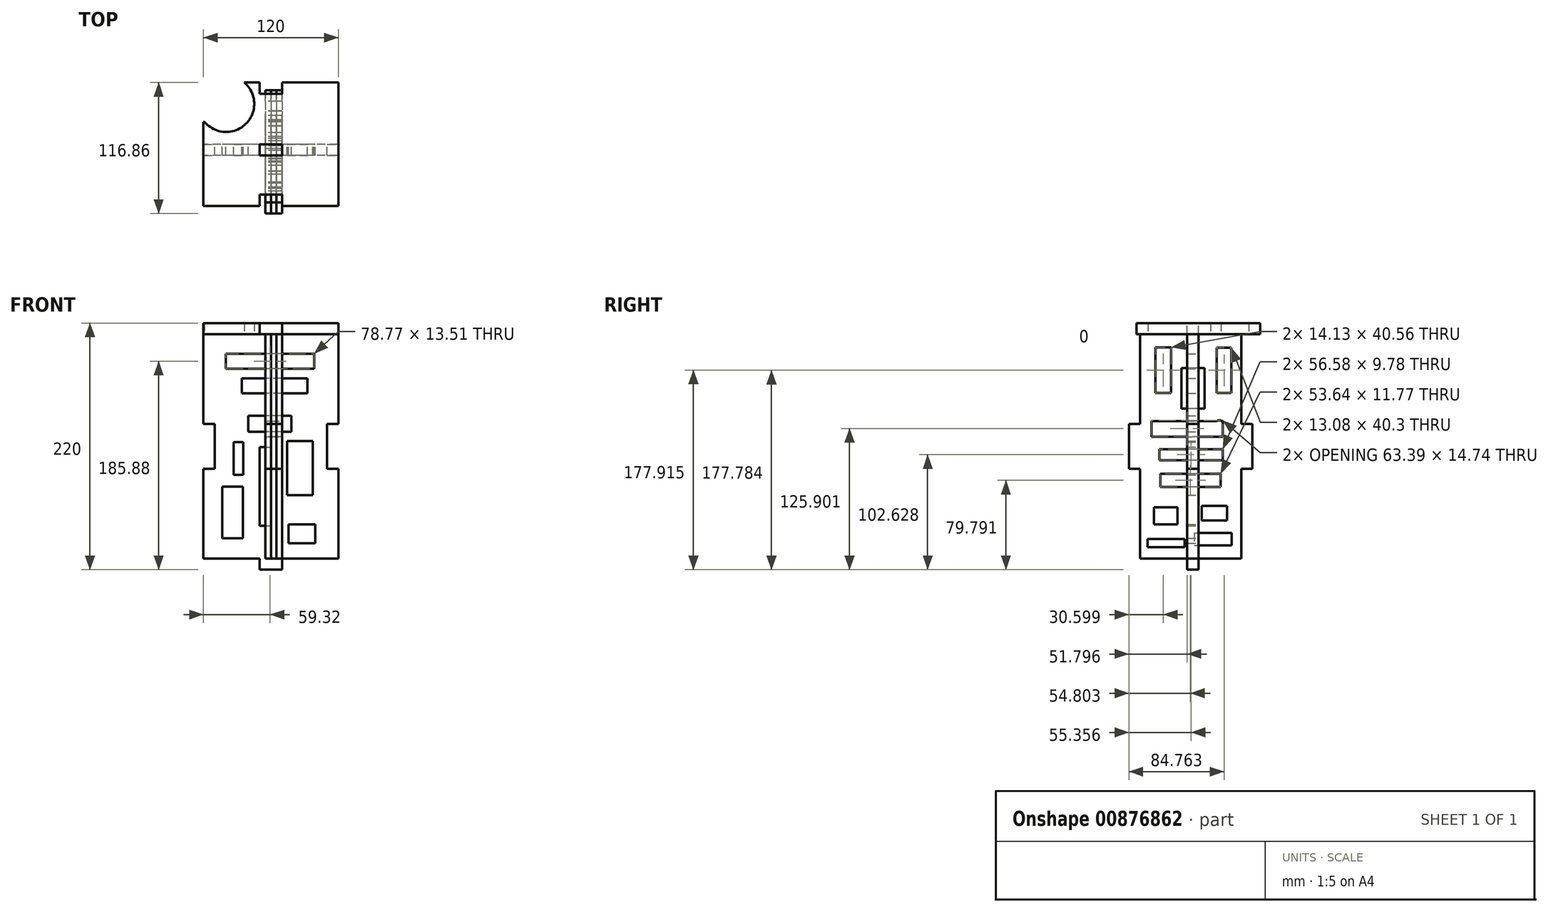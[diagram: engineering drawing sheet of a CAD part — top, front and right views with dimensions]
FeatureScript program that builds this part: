
annotation { "Feature Type Name" : "Feature", "Feature Type Description" : "" }
export const myFeature = defineFeature(function(context is Context, id is Id, definition is map)
    precondition{}
    {
        {
            var Q0;
            Q0=qCreatedBy(makeId("Top.planeOp"),FACE);
            var sketch = newSketch(context, id + "F0", { "sketchPlane" : qUnion([Q0])});
            skLineSegment(sketch, "E0.bottom", {"start": v(-60, -55) * mm, "end": v(-10, -55) * mm});
            skLineSegment(sketch, "E0.left", {"start": v(-60, -55) * mm, "end": v(-60, 21.17) * mm});
            skLineSegment(sketch, "E0.right", {"start": v(60, -55) * mm, "end": v(60, 55) * mm});
            skPoint(sketch, "E0.middle", {"position": v(0, 0) * mm});
            skLineSegment(sketch, "E1.bottom", {"start": v(-10, 45) * mm, "end": v(10, 45) * mm});
            skLineSegment(sketch, "E1.left", {"start": v(-10, 45) * mm, "end": v(-10, 55) * mm});
            skLineSegment(sketch, "E1.right", {"start": v(10, 45) * mm, "end": v(10, 55) * mm});
            skPoint(sketch, "E1.middle", {"position": v(0, 55) * mm});
            skPoint(sketch, "E1.top.end.orphan", {"position": v(10, 65) * mm});
            skPoint(sketch, "E2.orphan", {"position": v(-10, 65) * mm});
            skLineSegment(sketch, "E3.trimOffspring", {"start": v(10, 55) * mm, "end": v(60, 55) * mm});
            skLineSegment(sketch, "E4.bottom", {"start": v(-10, -45) * mm, "end": v(10, -45) * mm});
            skLineSegment(sketch, "E4.left", {"start": v(-10, -45) * mm, "end": v(-10, -55) * mm});
            skLineSegment(sketch, "E4.right", {"start": v(10, -45) * mm, "end": v(10, -55) * mm});
            skPoint(sketch, "E4.middle", {"position": v(0, -55) * mm});
            skPoint(sketch, "E5.orphan", {"position": v(10, -65) * mm});
            skPoint(sketch, "E6.orphan", {"position": v(-10, -65) * mm});
            skLineSegment(sketch, "E7.trimOffspring", {"start": v(10, -55) * mm, "end": v(60, -55) * mm});
            skLineSegment(sketch, "E8", {"start": v(-59.1, 20) * mm, "end": v(-60, 20) * mm});
            skArc(sketch, "E9.trimOffspring", {"start": v(-60, 21.17) * mm, "mid": v(-22.8, 17.63) * mm, "end": v(-23.66, 55) * mm});
            skLineSegment(sketch, "E10.trimOffspring", {"start": v(-23.66, 55) * mm, "end": v(-10, 55) * mm});
            skPoint(sketch, "E11.orphan", {"position": v(-25, 20) * mm});
            skPoint(sketch, "E0.top.start.orphan", {"position": v(-60, 55) * mm});
            skLineSegment(sketch, "E12", {"start": v(-23.66, 55) * mm, "end": v(-60, 55) * mm, "construction": true});
            skLineSegment(sketch, "E13", {"start": v(-60, 21.17) * mm, "end": v(-60, 55) * mm, "construction": true});
            skSolve(sketch);
        }
        {
            var Q0;
            {var subQ1=sQuery(id+"F0.wireOp",EDGE,"E0.bottom");Q0=makeQuery(id+"F0.imprint","IMPRINT",FACE,{"disambiguationData":[TD([[makeQuery(id+"F0.imprint","IMPRINT",EDGE,{"derivedFrom":subQ1}),1.0]])]});}
            extrude(context, id + "F1", {"entities" : qUnion([Q0]), "depth" : 10 * mm, "offsetDistance" : 25 * mm});
        }
        {
            var Q0;
            Q0=qCreatedBy(makeId("Front.planeOp"),FACE);
            var sketch = newSketch(context, id + "F2", { "sketchPlane" : qUnion([Q0])});
            skLineSegment(sketch, "E14.bottom", {"start": v(60, 0) * mm, "end": v(10, 0) * mm});
            skLineSegment(sketch, "E14.top", {"start": v(60, -200) * mm, "end": v(10, -200) * mm});
            skLineSegment(sketch, "E14.left", {"start": v(60, 0) * mm, "end": v(60, -80) * mm});
            skLineSegment(sketch, "E14.right", {"start": v(-60, 0) * mm, "end": v(-60, -80) * mm});
            skLineSegment(sketch, "E15.top", {"start": v(-10, 10) * mm, "end": v(10, 10) * mm});
            skLineSegment(sketch, "E15.left", {"start": v(-10, 0) * mm, "end": v(-10, 10) * mm});
            skLineSegment(sketch, "E15.right", {"start": v(10, 0) * mm, "end": v(10, 10) * mm});
            skPoint(sketch, "E15.middle", {"position": v(0, 0) * mm});
            skPoint(sketch, "E16.orphan", {"position": v(-10, -10) * mm});
            skPoint(sketch, "E17.orphan", {"position": v(10, -10) * mm});
            skLineSegment(sketch, "E18.top", {"start": v(-10, -210) * mm, "end": v(10, -210) * mm});
            skLineSegment(sketch, "E18.left", {"start": v(-10, -200) * mm, "end": v(-10, -210) * mm});
            skLineSegment(sketch, "E18.right", {"start": v(10, -200) * mm, "end": v(10, -210) * mm});
            skPoint(sketch, "E18.middle", {"position": v(0, -200) * mm});
            skPoint(sketch, "E19.orphan", {"position": v(10, -190) * mm});
            skPoint(sketch, "E20.orphan", {"position": v(-10, -190) * mm});
            skLineSegment(sketch, "E21.trimOffspring", {"start": v(-10, -200) * mm, "end": v(-60, -200) * mm});
            skLineSegment(sketch, "E22.trimOffspring", {"start": v(-10, 0) * mm, "end": v(-60, 0) * mm});
            skLineSegment(sketch, "E23.bottom", {"start": v(50, -80) * mm, "end": v(60, -80) * mm});
            skLineSegment(sketch, "E23.top", {"start": v(50, -120) * mm, "end": v(60, -120) * mm});
            skLineSegment(sketch, "E23.left", {"start": v(50, -80) * mm, "end": v(50, -120) * mm});
            skPoint(sketch, "E23.middle", {"position": v(60, -100) * mm});
            skLineSegment(sketch, "E24.trimOffspring", {"start": v(60, -120) * mm, "end": v(60, -200) * mm});
            skPoint(sketch, "E23.right.start.orphan", {"position": v(70, -80) * mm});
            skPoint(sketch, "E25.orphan", {"position": v(70, -120) * mm});
            skLineSegment(sketch, "E26.bottom", {"start": v(-60, -120) * mm, "end": v(-50, -120) * mm});
            skLineSegment(sketch, "E26.top", {"start": v(-60, -80) * mm, "end": v(-50, -80) * mm});
            skLineSegment(sketch, "E26.right", {"start": v(-50, -120) * mm, "end": v(-50, -80) * mm});
            skPoint(sketch, "E26.middle", {"position": v(-60, -100) * mm});
            skPoint(sketch, "E27.orphan", {"position": v(-70, -80) * mm});
            skPoint(sketch, "E28.orphan", {"position": v(-70, -120) * mm});
            skLineSegment(sketch, "E29.trimOffspring", {"start": v(-60, -120) * mm, "end": v(-60, -200) * mm});
            skLineSegment(sketch, "E30.bottom", {"start": v(38.7, -17.36) * mm, "end": v(-40.06, -17.36) * mm});
            skLineSegment(sketch, "E30.top", {"start": v(38.7, -30.88) * mm, "end": v(-40.06, -30.88) * mm});
            skLineSegment(sketch, "E30.left", {"start": v(38.7, -17.36) * mm, "end": v(38.7, -30.88) * mm});
            skLineSegment(sketch, "E30.right", {"start": v(-40.06, -17.36) * mm, "end": v(-40.06, -30.88) * mm});
            skLineSegment(sketch, "E31.bottom", {"start": v(32.44, -39.45) * mm, "end": v(-25.9, -39.45) * mm});
            skLineSegment(sketch, "E31.top", {"start": v(32.44, -52.63) * mm, "end": v(-25.9, -52.63) * mm});
            skLineSegment(sketch, "E31.left", {"start": v(32.44, -39.45) * mm, "end": v(32.44, -52.63) * mm});
            skLineSegment(sketch, "E31.right", {"start": v(-25.9, -39.45) * mm, "end": v(-25.9, -52.63) * mm});
            skLineSegment(sketch, "E32.bottom", {"start": v(18.27, -72.73) * mm, "end": v(-20.29, -72.73) * mm});
            skLineSegment(sketch, "E32.top", {"start": v(18.27, -86.9) * mm, "end": v(-20.29, -86.9) * mm});
            skLineSegment(sketch, "E32.left", {"start": v(18.27, -72.73) * mm, "end": v(18.27, -86.9) * mm});
            skLineSegment(sketch, "E32.right", {"start": v(-20.29, -72.73) * mm, "end": v(-20.29, -86.9) * mm});
            skLineSegment(sketch, "E33.bottom", {"start": v(-10.07, -100.75) * mm, "end": v(0, -100.75) * mm});
            skLineSegment(sketch, "E33.top", {"start": v(-10.07, -170.95) * mm, "end": v(0, -170.95) * mm});
            skLineSegment(sketch, "E33.left", {"start": v(-10.07, -100.75) * mm, "end": v(-10.07, -170.95) * mm});
            skLineSegment(sketch, "E33.right", {"start": v(0, -100.75) * mm, "end": v(0, -170.95) * mm});
            skLineSegment(sketch, "E34.bottom", {"start": v(14.32, -95.14) * mm, "end": v(37.39, -95.14) * mm});
            skLineSegment(sketch, "E34.top", {"start": v(14.32, -143.6) * mm, "end": v(37.39, -143.6) * mm});
            skLineSegment(sketch, "E34.left", {"start": v(14.32, -95.14) * mm, "end": v(14.32, -143.6) * mm});
            skLineSegment(sketch, "E34.right", {"start": v(37.39, -95.14) * mm, "end": v(37.39, -143.6) * mm});
            skLineSegment(sketch, "E35.bottom", {"start": v(-24.9, -136.01) * mm, "end": v(-43.36, -136.01) * mm});
            skLineSegment(sketch, "E35.top", {"start": v(-24.9, -181.82) * mm, "end": v(-43.36, -181.82) * mm});
            skLineSegment(sketch, "E35.left", {"start": v(-24.9, -136.01) * mm, "end": v(-24.9, -181.82) * mm});
            skLineSegment(sketch, "E35.right", {"start": v(-43.36, -136.01) * mm, "end": v(-43.36, -181.82) * mm});
            skLineSegment(sketch, "E36.bottom", {"start": v(39.36, -169.63) * mm, "end": v(15.63, -169.63) * mm});
            skLineSegment(sketch, "E36.top", {"start": v(39.36, -186.44) * mm, "end": v(15.63, -186.44) * mm});
            skLineSegment(sketch, "E36.left", {"start": v(39.36, -169.63) * mm, "end": v(39.36, -186.44) * mm});
            skLineSegment(sketch, "E36.right", {"start": v(15.63, -169.63) * mm, "end": v(15.63, -186.44) * mm});
            skLineSegment(sketch, "E37.bottom", {"start": v(-33.32, -96.04) * mm, "end": v(-24.61, -96.04) * mm});
            skLineSegment(sketch, "E37.top", {"start": v(-33.32, -125.28) * mm, "end": v(-24.61, -125.28) * mm});
            skLineSegment(sketch, "E37.left", {"start": v(-33.32, -96.04) * mm, "end": v(-33.32, -125.28) * mm});
            skLineSegment(sketch, "E37.right", {"start": v(-24.61, -96.04) * mm, "end": v(-24.61, -125.28) * mm});
            skSolve(sketch);
        }
        {
            var Q0;
            Q0 = qSketchRegion(id + "F2", true);
            extrude(context, id + "F3", {"entities" : qUnion([Q0]), "depth" : 10 * mm, "offsetDistance" : 25 * mm});
        }
        {
            var Q0;
            Q0=qCreatedBy(makeId("Right.planeOp"),FACE);
            var sketch = newSketch(context, id + "F4", { "sketchPlane" : qUnion([Q0])});
            skLineSegment(sketch, "E38.bottom", {"start": v(38.14, 0) * mm, "end": v(-51.86, 0) * mm});
            skLineSegment(sketch, "E38.top", {"start": v(38.14, -200) * mm, "end": v(-51.86, -200) * mm});
            skLineSegment(sketch, "E38.left", {"start": v(38.14, 0) * mm, "end": v(38.14, -80) * mm});
            skLineSegment(sketch, "E38.right", {"start": v(-51.86, 0) * mm, "end": v(-51.86, -80) * mm});
            skLineSegment(sketch, "E39", {"start": v(38.14, -80) * mm, "end": v(48.14, -80) * mm});
            skLineSegment(sketch, "E40", {"start": v(48.14, -80) * mm, "end": v(48.14, -120) * mm});
            skLineSegment(sketch, "E41", {"start": v(48.14, -120) * mm, "end": v(38.14, -120) * mm});
            skLineSegment(sketch, "E42.trimOffspring", {"start": v(38.14, -120) * mm, "end": v(38.14, -200) * mm});
            skLineSegment(sketch, "E43", {"start": v(-51.86, -80) * mm, "end": v(-61.86, -80) * mm});
            skLineSegment(sketch, "E44", {"start": v(-61.86, -80) * mm, "end": v(-61.86, -120) * mm});
            skLineSegment(sketch, "E45", {"start": v(-61.86, -120) * mm, "end": v(-51.86, -120) * mm});
            skLineSegment(sketch, "E46.trimOffspring", {"start": v(-51.86, -120) * mm, "end": v(-51.86, -200) * mm});
            skText(sketch, "E47", { "text": "YouSef", "fontName": "OpenSans-Regular.ttf"});
            skPoint(sketch, "E48.left.end.orphan", {"position": v(-15.86, -56.8) * mm});
            skPoint(sketch, "E49.bottom.start.orphan", {"position": v(-15.86, -107.95) * mm});
            skLineSegment(sketch, "E50.bottom", {"start": v(-41.76, -77.6) * mm, "end": v(21.63, -77.6) * mm});
            skLineSegment(sketch, "E50.top", {"start": v(-41.76, -91.28) * mm, "end": v(21.63, -91.28) * mm});
            skLineSegment(sketch, "E50.left", {"start": v(-41.76, -77.6) * mm, "end": v(-41.76, -91.28) * mm});
            skLineSegment(sketch, "E50.right", {"start": v(21.63, -77.6) * mm, "end": v(21.63, -91.28) * mm});
            skLineSegment(sketch, "E51.bottom", {"start": v(29.45, -12.07) * mm, "end": v(16.36, -12.07) * mm});
            skLineSegment(sketch, "E51.top", {"start": v(29.45, -52.36) * mm, "end": v(16.36, -52.36) * mm});
            skLineSegment(sketch, "E51.left", {"start": v(29.45, -12.07) * mm, "end": v(29.45, -52.36) * mm});
            skLineSegment(sketch, "E51.right", {"start": v(16.36, -12.07) * mm, "end": v(16.36, -52.36) * mm});
            skLineSegment(sketch, "E52.bottom", {"start": v(-38.33, -11.8) * mm, "end": v(-24.2, -11.8) * mm});
            skLineSegment(sketch, "E52.top", {"start": v(-38.33, -52.36) * mm, "end": v(-24.2, -52.36) * mm});
            skLineSegment(sketch, "E52.left", {"start": v(-38.33, -11.8) * mm, "end": v(-38.33, -52.36) * mm});
            skLineSegment(sketch, "E52.right", {"start": v(-24.2, -11.8) * mm, "end": v(-24.2, -52.36) * mm});
            skLineSegment(sketch, "E53.bottom", {"start": v(5.37, -30.12) * mm, "end": v(-15.04, -30.12) * mm});
            skLineSegment(sketch, "E53.top", {"start": v(5.37, -66.5) * mm, "end": v(-15.04, -66.5) * mm});
            skLineSegment(sketch, "E53.left", {"start": v(5.37, -30.12) * mm, "end": v(5.37, -66.5) * mm});
            skLineSegment(sketch, "E53.right", {"start": v(-15.04, -30.12) * mm, "end": v(-15.04, -66.5) * mm});
            skLineSegment(sketch, "E54.bottom", {"start": v(19.76, -124.32) * mm, "end": v(-33.88, -124.32) * mm});
            skLineSegment(sketch, "E54.top", {"start": v(19.76, -136.1) * mm, "end": v(-33.88, -136.1) * mm});
            skLineSegment(sketch, "E54.left", {"start": v(19.76, -124.32) * mm, "end": v(19.76, -136.1) * mm});
            skLineSegment(sketch, "E54.right", {"start": v(-33.88, -124.32) * mm, "end": v(-33.88, -136.1) * mm});
            skLineSegment(sketch, "E55.bottom", {"start": v(25.52, -153.1) * mm, "end": v(3.02, -153.1) * mm});
            skLineSegment(sketch, "E55.top", {"start": v(25.52, -165.93) * mm, "end": v(3.02, -165.93) * mm});
            skLineSegment(sketch, "E55.left", {"start": v(25.52, -153.1) * mm, "end": v(25.52, -165.93) * mm});
            skLineSegment(sketch, "E55.right", {"start": v(3.02, -153.1) * mm, "end": v(3.02, -165.93) * mm});
            skLineSegment(sketch, "E56.bottom", {"start": v(-18.7, -154.41) * mm, "end": v(-39.63, -154.41) * mm});
            skLineSegment(sketch, "E56.top", {"start": v(-18.7, -169.59) * mm, "end": v(-39.63, -169.59) * mm});
            skLineSegment(sketch, "E56.left", {"start": v(-18.7, -154.41) * mm, "end": v(-18.7, -169.59) * mm});
            skLineSegment(sketch, "E56.right", {"start": v(-39.63, -154.41) * mm, "end": v(-39.63, -169.59) * mm});
            skLineSegment(sketch, "E57.bottom", {"start": v(-3.79, -177.18) * mm, "end": v(29.7, -177.18) * mm});
            skLineSegment(sketch, "E57.top", {"start": v(-3.79, -188.17) * mm, "end": v(29.7, -188.17) * mm});
            skLineSegment(sketch, "E57.left", {"start": v(-3.79, -177.18) * mm, "end": v(-3.79, -188.17) * mm});
            skLineSegment(sketch, "E57.right", {"start": v(29.7, -177.18) * mm, "end": v(29.7, -188.17) * mm});
            skLineSegment(sketch, "E58.bottom", {"start": v(-45.4, -182.67) * mm, "end": v(-12.42, -182.67) * mm});
            skLineSegment(sketch, "E58.top", {"start": v(-45.4, -190) * mm, "end": v(-12.42, -190) * mm});
            skLineSegment(sketch, "E58.left", {"start": v(-45.4, -182.67) * mm, "end": v(-45.4, -190) * mm});
            skLineSegment(sketch, "E58.right", {"start": v(-12.42, -182.67) * mm, "end": v(-12.42, -190) * mm});
            skLineSegment(sketch, "E59.bottom", {"start": v(21.79, -102.48) * mm, "end": v(-34.8, -102.48) * mm});
            skLineSegment(sketch, "E59.top", {"start": v(21.79, -112.26) * mm, "end": v(-34.8, -112.26) * mm});
            skLineSegment(sketch, "E59.left", {"start": v(21.79, -102.48) * mm, "end": v(21.79, -112.26) * mm});
            skLineSegment(sketch, "E59.right", {"start": v(-34.8, -102.48) * mm, "end": v(-34.8, -112.26) * mm});
            const initialGuessF4  = {"E47": [-0.04176, -0.09128, 1, 0, 0.01369]};
            skSetInitialGuess(sketch, initialGuessF4);
            skSolve(sketch);
        }
        {
            var Q0;
            Q0=makeQuery(id+"F4.imprint","IMPRINT",FACE,{"disambiguationData":[TD([[makeQuery(id+"F4.imprint","IMPRINT",EDGE,{"derivedFrom":sQuery(id+"F4.wireOp",EDGE,"E38.bottom")}),1.0]])]});
            extrude(context, id + "F5", {"entities" : qUnion([Q0]), "depth" : 10 * mm, "offsetDistance" : 25 * mm});
        }
        {
            var Q0;
            Q0=makeQuery(id+"F4.imprint","IMPRINT",FACE,{"disambiguationData":[TD([[makeQuery(id+"F4.imprint","IMPRINT",EDGE,{"derivedFrom":sQuery(id+"F4.wireOp",EDGE,"E38.bottom")}),1.0]])]});
            extrude(context, id + "F6", {"entities" : qUnion([Q0]), "endBound" : BoundingType.SYMMETRIC, "depth" : 10 * mm, "offsetDistance" : 25 * mm});
        }
    });
